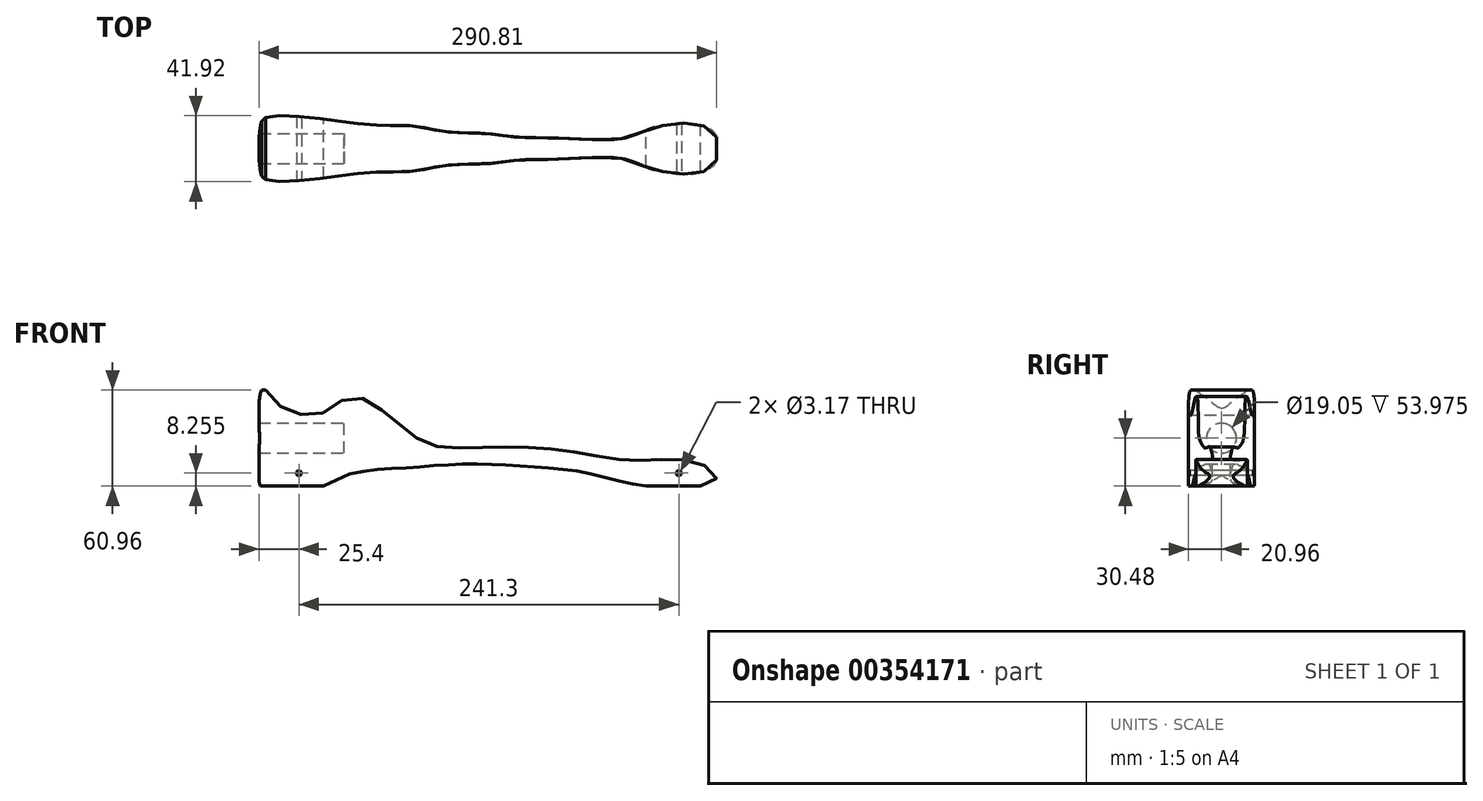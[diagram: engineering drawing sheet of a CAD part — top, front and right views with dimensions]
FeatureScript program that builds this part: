
annotation { "Feature Type Name" : "Feature", "Feature Type Description" : "" }
export const myFeature = defineFeature(function(context is Context, id is Id, definition is map)
    precondition{}
    {
        {
            var Q0;
            Q0=qCreatedBy(makeId("Front.planeOp"),FACE);
            var sketch = newSketch(context, id + "F0", { "sketchPlane" : qUnion([Q0])});
            skLineSegment(sketch, "E0.bottom", {"start": v(-146.05, 31.75) * mm, "end": v(146.05, 31.75) * mm, "construction": true});
            skLineSegment(sketch, "E0.top", {"start": v(-146.05, -31.75) * mm, "end": v(146.05, -31.75) * mm, "construction": true});
            skLineSegment(sketch, "E0.right", {"start": v(146.05, 31.75) * mm, "end": v(146.05, -31.75) * mm, "construction": true});
            skFitSpline(sketch, "E1", {"points": [v(-146.05, -24.02) * mm, v(-146.05, 0) * mm, v(-146.05, 18.94) * mm, v(-143.37, 31.04) * mm, v(-133.99, 21.8) * mm, v(-126.47, 16.79) * mm, v(-106.12, 15.85) * mm, v(-84.82, 26.5) * mm, v(-45.54, 0) * mm, v(-21.45, -6.25) * mm, v(7.78, -5.73) * mm, v(33.01, -6.25) * mm, v(60.45, -9.94) * mm, v(87.84, -13.9) * mm, v(110.75, -13.63) * mm, v(132.78, -15.2) * mm, v(139.9, -19.28) * mm, v(144.61, -23.32) * mm, v(143.84, -26.97) * mm, v(140.96, -29.08) * mm, v(115.4, -31.75) * mm, v(84.67, -27.52) * mm, v(61.22, -21.8) * mm, v(40.84, -19.28) * mm, v(10.3, -17.05) * mm, v(-22.07, -16.66) * mm, v(-50.4, -18.66) * mm, v(-72.33, -19.99) * mm, v(-94.48, -25.08) * mm, v(-102.58, -29.9) * mm, v(-137.5, -31.75) * mm, v(-144.78, -30.62) * mm, v(-146.05, -24.02) * mm]});
            skLineSegment(sketch, "E2.bottom", {"start": v(-146.05, 9.52) * mm, "end": v(-95.25, 9.52) * mm, "construction": true});
            skLineSegment(sketch, "E2.top", {"start": v(-141.83, -9.52) * mm, "end": v(-95.25, -9.52) * mm, "construction": true});
            skLineSegment(sketch, "E2.right", {"start": v(-95.25, 9.52) * mm, "end": v(-95.25, -9.52) * mm, "construction": true});
            skLineSegment(sketch, "E3", {"start": v(-146.05, 31.75) * mm, "end": v(-146.05, -31.75) * mm, "construction": true});
            skSolve(sketch);
        }
        {
            var Q0;
            Q0=qCreatedBy(makeId("Top.planeOp"),FACE);
            var sketch = newSketch(context, id + "F1", { "sketchPlane" : qUnion([Q0])});
            skLineSegment(sketch, "E4.bottom", {"start": v(-146.05, 22.22) * mm, "end": v(146.05, 22.23) * mm, "construction": true});
            skLineSegment(sketch, "E4.top", {"start": v(-146.05, -22.23) * mm, "end": v(146.05, -22.22) * mm, "construction": true});
            skLineSegment(sketch, "E4.left", {"start": v(-146.05, 22.22) * mm, "end": v(-146.05, -22.23) * mm, "construction": true});
            skLineSegment(sketch, "E4.right", {"start": v(146.05, 22.22) * mm, "end": v(146.05, -22.22) * mm, "construction": true});
            skLineSegment(sketch, "E5", {"start": v(-146.05, 0) * mm, "end": v(146.05, 0) * mm, "construction": true});
            skFitSpline(sketch, "E6", {"points": [v(-146.05, 0) * mm, v(-144.7, 15.87) * mm, v(-143.15, 18.58) * mm, v(-139.45, 20.44) * mm, v(-116.48, 20.05) * mm, v(-93.03, 17.08) * mm, v(-73.1, 14.96) * mm, v(-46.23, 14.17) * mm, v(-32.68, 11.43) * mm, v(-11.35, 9.85) * mm, v(1.14, 9.38) * mm, v(16.15, 7.48) * mm, v(35.6, 6.85) * mm, v(61.1, 5.95) * mm, v(86.4, 6.74) * mm, v(103.78, 12.99) * mm, v(130.49, 15.99) * mm, v(141.35, 12.02) * mm, v(143.98, 9.01) * mm, v(146.05, 0) * mm], "startDerivative": vector(0, 335.54) * mm, "endDerivative": vector(0, -277.49) * mm});
            skFitSpline(sketch, "E7.MirrorCS", {"points": [v(-146.05, 0) * mm, v(-144.7, -15.87) * mm, v(-143.15, -18.58) * mm, v(-139.45, -20.44) * mm, v(-116.48, -20.05) * mm, v(-93.03, -17.08) * mm, v(-73.1, -14.96) * mm, v(-46.23, -14.17) * mm, v(-32.68, -11.43) * mm, v(-11.35, -9.85) * mm, v(1.14, -9.38) * mm, v(16.15, -7.48) * mm, v(35.6, -6.85) * mm, v(61.1, -5.95) * mm, v(86.4, -6.74) * mm, v(103.78, -12.99) * mm, v(130.49, -15.99) * mm, v(141.35, -12.02) * mm, v(143.98, -9.01) * mm, v(146.05, 0) * mm], "startDerivative": vector(0, -335.54) * mm, "endDerivative": vector(0, 277.49) * mm});
            skLineSegment(sketch, "E8.MirrorCS", {"start": v(-146.05, -22.23) * mm, "end": v(146.05, -22.23) * mm});
            skSolve(sketch);
        }
        {
            var Q0;
            Q0=qCreatedBy(makeId("Right.planeOp"),FACE);
            var sketch = newSketch(context, id + "F2", { "sketchPlane" : qUnion([Q0])});
            skCircle(sketch, "E9", {"center": v(0, 0) * mm, "radius": 9.53 * mm});
            skSolve(sketch);
        }
        {
            var Q0;
            Q0=qCreatedBy(makeId("Front.planeOp"),FACE);
            var sketch = newSketch(context, id + "F3", { "sketchPlane" : qUnion([Q0])});
            skCircle(sketch, "E10", {"center": v(-120.65, -22.22) * mm, "radius": 1.59 * mm});
            skCircle(sketch, "E11", {"center": v(120.65, -22.23) * mm, "radius": 1.59 * mm});
            skSolve(sketch);
        }
        {
            var Q0;
            Q0=qSketchRegion(id+"F0",true);
            extrude(context, id + "F4", {"entities" : qUnion([Q0]), "depth" : 44.45 * mm, "symmetric" : true});
        }
        {
            var Q0;
            Q0=qSketchRegion(id+"F1",true);
            extrude(context, id + "F5", {"entities" : qUnion([Q0]), "operationType" : NewBodyOperationType.INTERSECT, "oppositeDirection" : true, "depth" : 60.96 * mm, "symmetric" : true});
        }
        {
            var Q0;
            Q0=qSketchRegion(id+"F2",true);
            extrude(context, id + "F6", {"entities" : qUnion([Q0]), "operationType" : NewBodyOperationType.REMOVE, "oppositeDirection" : true, "depth" : 152.4 * mm, "hasSecondDirection" : true, "secondDirectionOppositeDirection" : true, "secondDirectionDepth" : 92.07 * mm});
        }
        {
            var Q0;
            Q0=qSketchRegion(id+"F3",true);
            extrude(context, id + "F7", {"entities" : qUnion([Q0]), "operationType" : NewBodyOperationType.REMOVE, "oppositeDirection" : true, "depth" : 50.8 * mm, "symmetric" : true});
        }
    });
